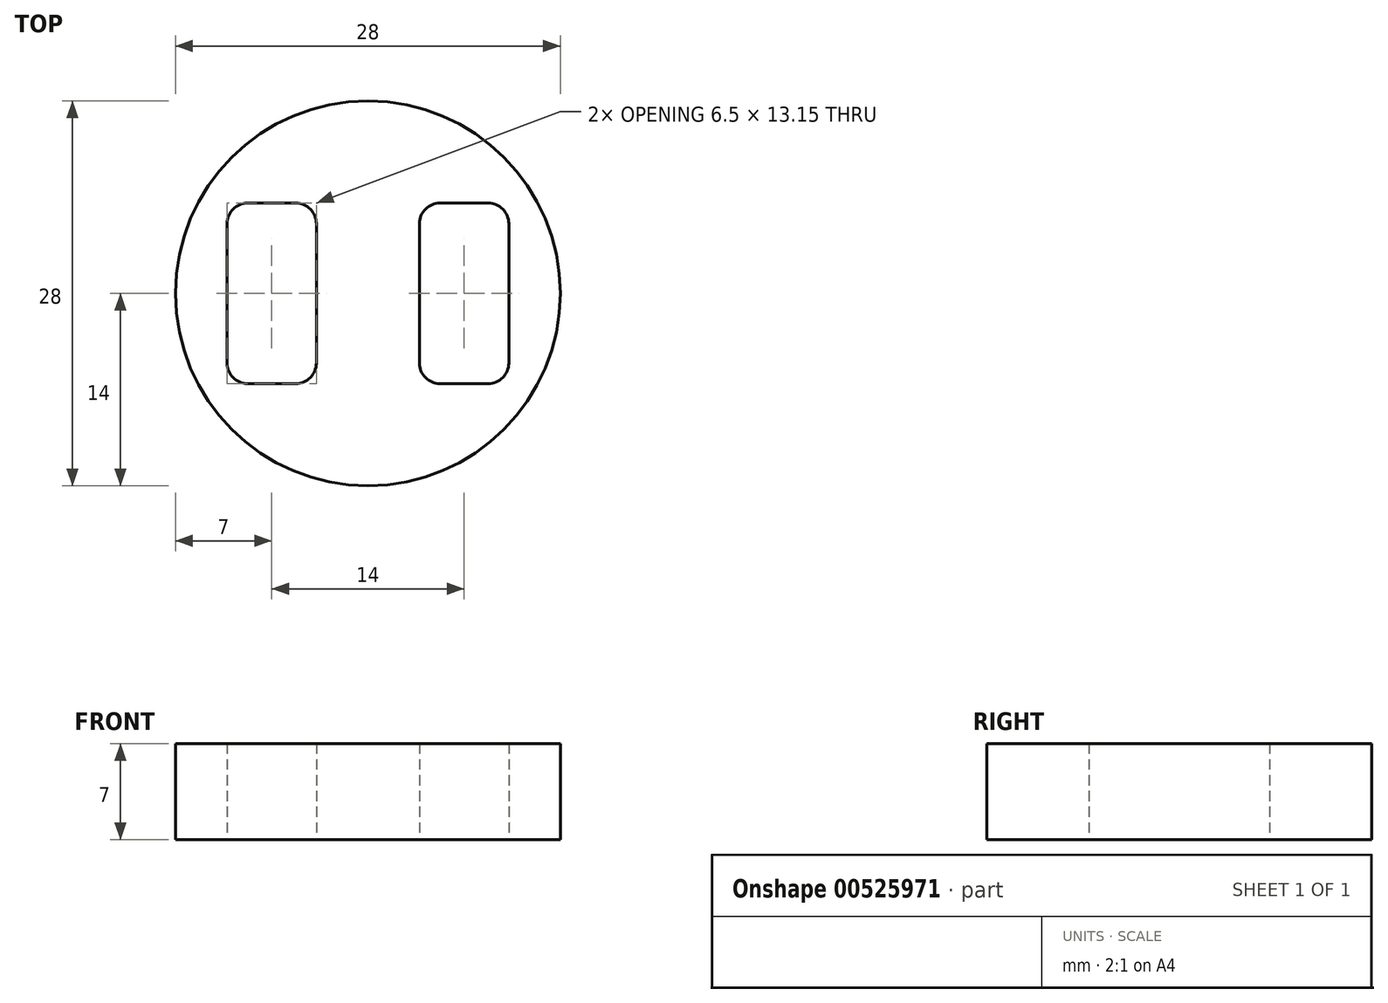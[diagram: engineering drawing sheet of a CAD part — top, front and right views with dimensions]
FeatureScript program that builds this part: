
annotation { "Feature Type Name" : "Feature", "Feature Type Description" : "" }
export const myFeature = defineFeature(function(context is Context, id is Id, definition is map)
    precondition{}
    {
        {
            var Q0;
            Q0=qCreatedBy(makeId("Top.planeOp"),FACE);
            var sketch = newSketch(context, id + "F0", { "sketchPlane" : qUnion([Q0])});
            skCircle(sketch, "E0", {"center": v(0, 0) * mm, "radius": 14 * mm});
            skLineSegment(sketch, "E1.bottom", {"start": v(-5.25, 6.57) * mm, "end": v(-8.75, 6.57) * mm});
            skLineSegment(sketch, "E1.top", {"start": v(-5.25, -6.57) * mm, "end": v(-8.75, -6.57) * mm});
            skLineSegment(sketch, "E1.left", {"start": v(-3.75, 5.07) * mm, "end": v(-3.75, -5.07) * mm});
            skLineSegment(sketch, "E1.right", {"start": v(-10.25, 5.07) * mm, "end": v(-10.25, -5.07) * mm});
            skPoint(sketch, "E1.middle", {"position": v(-7, 0) * mm});
            skPoint(sketch, "E2.visualSharp", {"position": v(-10.25, 6.57) * mm});
            skArc(sketch, "E2.filletArc", {"start": v(-8.75, 6.57) * mm, "mid": v(-9.81, 6.13) * mm, "end": v(-10.25, 5.07) * mm});
            skPoint(sketch, "E3.visualSharp", {"position": v(-3.75, 6.57) * mm});
            skArc(sketch, "E3.filletArc", {"start": v(-3.75, 5.07) * mm, "mid": v(-4.19, 6.13) * mm, "end": v(-5.25, 6.57) * mm});
            skPoint(sketch, "E4.visualSharp", {"position": v(-3.75, -6.57) * mm});
            skArc(sketch, "E4.filletArc", {"start": v(-5.25, -6.57) * mm, "mid": v(-4.19, -6.13) * mm, "end": v(-3.75, -5.07) * mm});
            skPoint(sketch, "E5.visualSharp", {"position": v(-10.25, -6.57) * mm});
            skArc(sketch, "E5.filletArc", {"start": v(-10.25, -5.07) * mm, "mid": v(-9.81, -6.13) * mm, "end": v(-8.75, -6.57) * mm});
            skArc(sketch, "E6.MirrorCS", {"start": v(10.25, -5.07) * mm, "mid": v(9.81, -6.13) * mm, "end": v(8.75, -6.57) * mm});
            skArc(sketch, "E7.MirrorCS", {"start": v(5.25, -6.57) * mm, "mid": v(4.19, -6.13) * mm, "end": v(3.75, -5.07) * mm});
            skArc(sketch, "E8.MirrorCS", {"start": v(3.75, 5.07) * mm, "mid": v(4.19, 6.13) * mm, "end": v(5.25, 6.57) * mm});
            skArc(sketch, "E9.MirrorCS", {"start": v(8.75, 6.57) * mm, "mid": v(9.81, 6.13) * mm, "end": v(10.25, 5.07) * mm});
            skPoint(sketch, "E10.MirrorP", {"position": v(10.25, -6.57) * mm});
            skPoint(sketch, "E11.MirrorP", {"position": v(3.75, -6.57) * mm});
            skLineSegment(sketch, "E12.MirrorCS", {"start": v(5.25, 6.57) * mm, "end": v(8.75, 6.57) * mm});
            skPoint(sketch, "E13.MirrorP", {"position": v(3.75, 6.57) * mm});
            skLineSegment(sketch, "E14.MirrorCS", {"start": v(5.25, -6.57) * mm, "end": v(8.75, -6.57) * mm});
            skLineSegment(sketch, "E15.MirrorCS", {"start": v(10.25, 5.07) * mm, "end": v(10.25, -5.07) * mm});
            skLineSegment(sketch, "E16.MirrorCS", {"start": v(3.75, 5.07) * mm, "end": v(3.75, -5.07) * mm});
            skPoint(sketch, "E17.MirrorP", {"position": v(10.25, 6.57) * mm});
            skPoint(sketch, "E18.MirrorP", {"position": v(7, 0) * mm});
            skSolve(sketch);
        }
        {
            var Q0;
            Q0=makeQuery(id+"F0.imprint","IMPRINT",FACE,{"disambiguationData":[TD([[makeQuery(id+"F0.imprint","IMPRINT",EDGE,{"derivedFrom":sQuery(id+"F0.wireOp",EDGE,"E0")}),1.0]])]});
            extrude(context, id + "F1", {"entities" : qUnion([Q0]), "depth" : 7 * mm, "offsetDistance" : 25 * mm});
        }
    });
